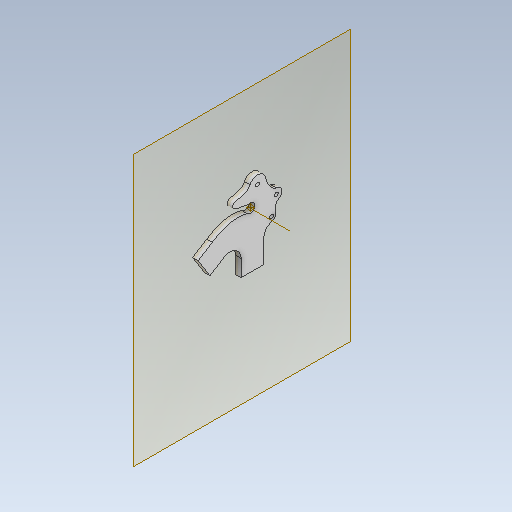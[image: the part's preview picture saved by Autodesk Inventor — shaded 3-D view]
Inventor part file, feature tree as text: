
AUTODESK INVENTOR PART (.ipt)
format: ipt  version: 2021 (Build 250183000, 183)  size: 181,760 bytes
history: native  units: mm
features: other x9, reference x6, sketch x2, plane x1, extrude x1, hole x1
ambient origin geometry x8: Origin, YZ Plane, XZ Plane, XY Plane, X Axis, Y Axis, Z Axis, Center Point
bodies: Body1 (feature_tree)
feature tree (20):
  other  "Sólido1"
  plane  "Plano de trabajo1"
  extrude  "Extrusión1"  TaperAngle=60.0deg  [1 undecoded]
  hole  "Agujero1"  [1 undecoded]
  other  "Punto de trabajo1"
  sketch  "Boceto1"  dims[d75=20.0mm d76=60.0deg]
  reference  "Referencia1"
  reference  "Referencia2"
  reference  "Referencia3"
  reference  "Referencia4"
  reference  "Referencia5"
  reference  "Referencia6"
  sketch  "Boceto2"  dims[d77=15.0mm d78=8.0mm d232=15.0mm d233=10.0mm d234=8.0mm d286=5.0mm d287=0.0mm d290=0.349066mm d291=50.0mm d292=3.4mm d293=6.0mm d294=6.3mm d295=2.0mm d296=90.0deg d297=8.0mm d298=20.594885mm]
  other  "Eje de trabajo1"
  parser-record x1  (decoder bookkeeping rows leaked as tree rows — omitted from the tree; the rows remain in map.json)
  other  "Marco_Bicicleta.iam"
  other  "Esqueleto_estructura:1"
  other  "Estructura 1617045494032:1"
  other  "ANSI  1617061874634:1"
  other  "ANSI  1618003984630:1"
note: 2 required parameter values undecoded (feature->parameter linkage not recoverable at this tier; creation-order binding heuristic only, values carry confidence <= 0.55)
note: 1 file-system path scrubbed to <path> (originals preserved in map.json)
